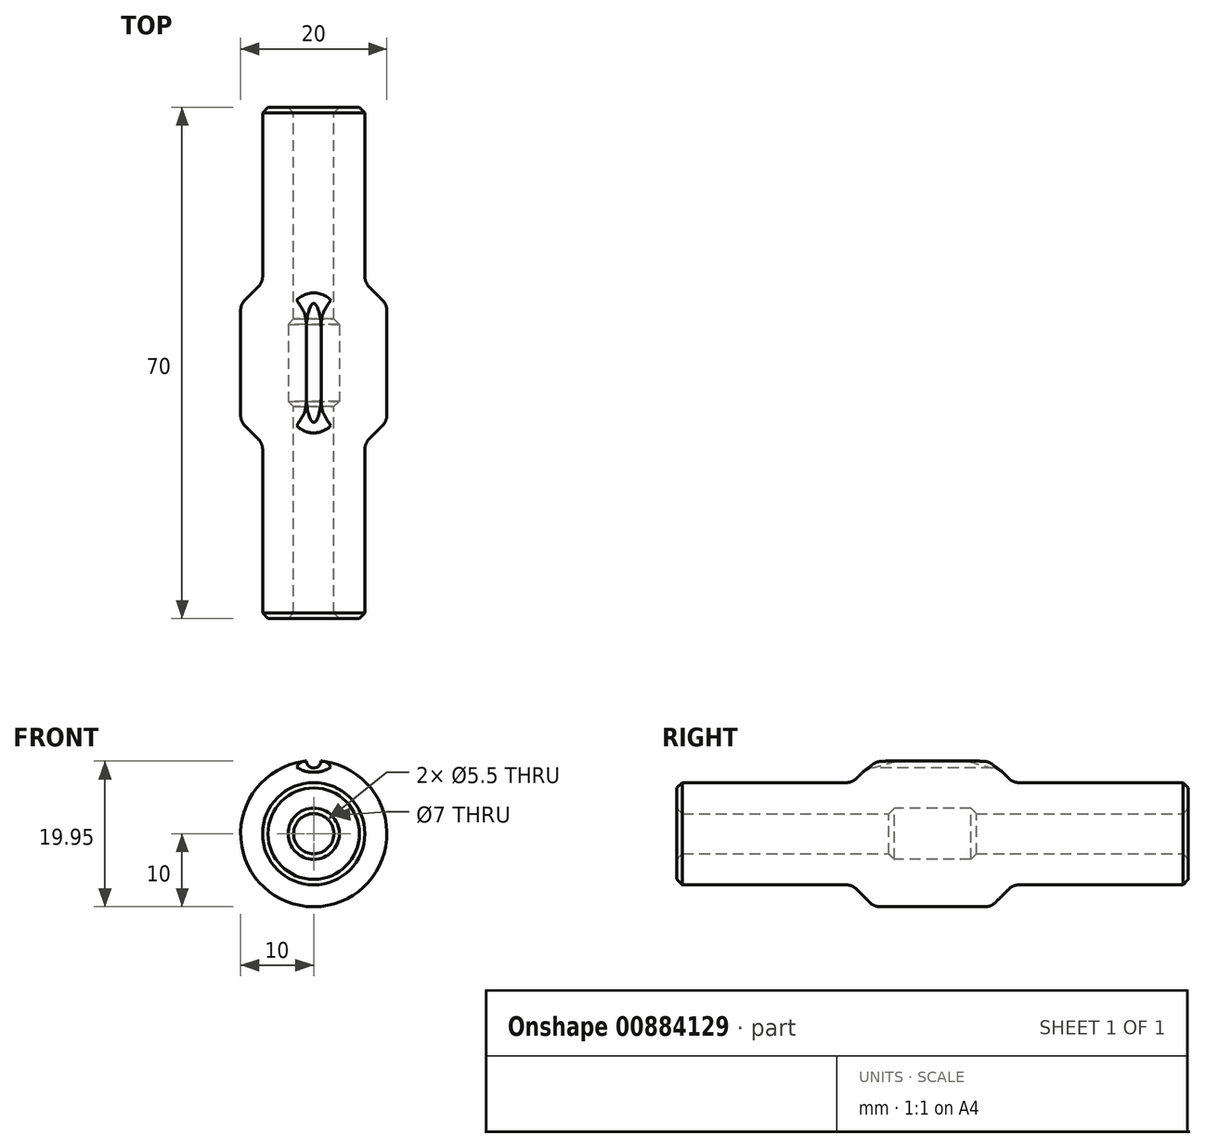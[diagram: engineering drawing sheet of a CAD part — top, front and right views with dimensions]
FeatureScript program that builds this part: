
annotation { "Feature Type Name" : "Feature", "Feature Type Description" : "" }
export const myFeature = defineFeature(function(context is Context, id is Id, definition is map)
    precondition{}
    {
        {
            var Q0;
            Q0=qCreatedBy(makeId("Front.planeOp"),FACE);
            var sketch = newSketch(context, id + "F0", { "sketchPlane" : qUnion([Q0])});
            skCircle(sketch, "E0", {"center": v(0, 0) * mm, "radius": 7 * mm});
            skCircle(sketch, "E1", {"center": v(0, 0) * mm, "radius": 2.75 * mm});
            skSolve(sketch);
        }
        {
            var Q0;
            Q0 = qSketchRegion(id + "F0", true);
            extrude(context, id + "F1", {"entities" : qUnion([Q0]), "endBound" : BoundingType.SYMMETRIC, "depth" : 70 * mm, "offsetDistance" : 25.4 * mm});
        }
        {
            var Q0;
            Q0=qCreatedBy(makeId("Front.planeOp"),FACE);
            var sketch = newSketch(context, id + "F2", { "sketchPlane" : qUnion([Q0])});
            skCircle(sketch, "E2", {"center": v(0, 0) * mm, "radius": 10 * mm});
            skCircle(sketch, "E3.0", {"center": v(0, 0) * mm, "radius": 2.75 * mm});
            skSolve(sketch);
        }
        {
            var Q0;
            Q0 = qSketchRegion(id + "F2", true);
            extrude(context, id + "F3", {"entities" : qUnion([Q0]), "operationType" : NewBodyOperationType.ADD, "endBound" : BoundingType.SYMMETRIC, "depth" : 16 * mm, "offsetDistance" : 25.4 * mm});
        }
        {
            var Q0;
            Q0=qCreatedBy(makeId("Front.planeOp"),FACE);
            var sketch = newSketch(context, id + "F4", { "sketchPlane" : qUnion([Q0])});
            skCircle(sketch, "E4.0", {"center": v(0, 0) * mm, "radius": 3.5 * mm});
            skSolve(sketch);
        }
        {
            var Q0;
            Q0 = qSketchRegion(id + "F4", true);
            var Q1;
            Q1=makeQuery(id+"F3.opExtrude","CAP_FACE",FACE,{"disambiguationData":[OSD([sQuery(id+"F2.wireOp",EDGE,"E2"),sQuery(id+"F2.wireOp",EDGE,"E3.0")])],"isStart":true});
            extrude(context, id + "F5", {"entities" : qUnion([Q0]), "operationType" : NewBodyOperationType.REMOVE, "endBound" : BoundingType.SYMMETRIC, "oppositeDirection" : true, "depth" : 12 * mm, "endBoundEntityFace" : qUnion([Q1]), "offsetDistance" : 25.4 * mm});
        }
        {
            var Q0;
            Q0=makeQuery(id+"F3.boolean.opBoolean","INTERSECT",EDGE,{"derivedFrom":[makeQuery(id+"F1.opExtrude","SWEPT_FACE",FACE,{"disambiguationData":[OSD([sQuery(id+"F0.wireOp",EDGE,"E0")])]}),makeQuery(id+"F3.opExtrude","CAP_FACE",FACE,{"disambiguationData":[OSD([sQuery(id+"F2.wireOp",EDGE,"E2"),sQuery(id+"F2.wireOp",EDGE,"E3.0")])],"isStart":false})]});
            var Q1;
            Q1=makeQuery(id+"F3.boolean.opBoolean","INTERSECT",EDGE,{"derivedFrom":[makeQuery(id+"F1.opExtrude","SWEPT_FACE",FACE,{"disambiguationData":[OSD([sQuery(id+"F0.wireOp",EDGE,"E0")])]}),makeQuery(id+"F3.opExtrude","CAP_FACE",FACE,{"disambiguationData":[OSD([sQuery(id+"F2.wireOp",EDGE,"E2"),sQuery(id+"F2.wireOp",EDGE,"E3.0")])],"isStart":true})]});
            chamfer(context, id + "F6", {"entities" : qUnion([Q0, Q1]), "width" : 3 * mm, "tangentPropagation" : true});
        }
        {
            var Q0;
            Q0=makeQuery(id+"F1.opExtrude","CAP_FACE",FACE,{"disambiguationData":[OSD([sQuery(id+"F0.wireOp",EDGE,"E0"),sQuery(id+"F0.wireOp",EDGE,"E1")])],"isStart":false});
            var sketch = newSketch(context, id + "F7", { "sketchPlane" : qUnion([Q0])});
            skCircle(sketch, "E5", {"center": v(0, 10) * mm, "radius": 1 * mm});
            skSolve(sketch);
        }
        {
            var Q0;
            Q0 = qSketchRegion(id + "F7", true);
            var Q1;
            Q1=makeQuery(id+"F3.opExtrude","CAP_FACE",FACE,{"disambiguationData":[OSD([sQuery(id+"F2.wireOp",EDGE,"E2"),sQuery(id+"F2.wireOp",EDGE,"E3.0")])],"isStart":true});
            var Q2;
            Q2=makeQuery(id+"F3.opExtrude","CAP_FACE",FACE,{"disambiguationData":[OSD([sQuery(id+"F2.wireOp",EDGE,"E2"),sQuery(id+"F2.wireOp",EDGE,"E3.0")])],"isStart":false});
            extrude(context, id + "F8", {"entities" : qUnion([Q0]), "operationType" : NewBodyOperationType.REMOVE, "endBound" : BoundingType.THROUGH_ALL, "oppositeDirection" : true, "depth" : 25.4 * mm, "endBoundEntityFace" : qUnion([Q1]), "offsetDistance" : 25.4 * mm});
        }
        {
            var Q0;
            Q0=makeQuery(id+"F1.opExtrude","CAP_EDGE",EDGE,{"disambiguationData":[OSD([sQuery(id+"F0.wireOp",EDGE,"E1")])],"isStart":false});
            var Q1;
            Q1=makeQuery(id+"F1.opExtrude","CAP_EDGE",EDGE,{"disambiguationData":[OSD([sQuery(id+"F0.wireOp",EDGE,"E1")])],"isStart":true});
            var Q2;
            Q2=makeQuery(id+"F5.boolean.opBoolean","COPY",EDGE,{"derivedFrom":makeQuery(id+"F5.opExtrude","CAP_EDGE",EDGE,{"disambiguationData":[OSD([sQuery(id+"F4.wireOp",EDGE,"E4.0")])],"isStart":true})});
            var Q3;
            Q3=makeQuery(id+"F5.boolean.opBoolean","COPY",EDGE,{"derivedFrom":makeQuery(id+"F5.opExtrude","CAP_EDGE",EDGE,{"disambiguationData":[OSD([sQuery(id+"F4.wireOp",EDGE,"E4.0")])],"isStart":false})});
            var Q4;
            Q4=makeQuery(id+"F1.opExtrude","CAP_EDGE",EDGE,{"disambiguationData":[OSD([sQuery(id+"F0.wireOp",EDGE,"E0")])],"isStart":false});
            var Q5;
            Q5=makeQuery(id+"F1.opExtrude","CAP_EDGE",EDGE,{"disambiguationData":[OSD([sQuery(id+"F0.wireOp",EDGE,"E0")])],"isStart":true});
            chamfer(context, id + "F9", {"entities" : qUnion([Q0, Q1, Q2, Q3, Q4, Q5]), "width" : .75 * mm, "tangentPropagation" : true});
        }
        {
            var Q0;
            {var subQ0=sQuery(id+"F0.wireOp",EDGE,"E0");var subQ1=makeQuery(id+"F3.opExtrude","CAP_FACE",FACE,{"disambiguationData":[OSD([sQuery(id+"F2.wireOp",EDGE,"E2"),sQuery(id+"F2.wireOp",EDGE,"E3.0")])],"isStart":false});var subQ2=makeQuery(id+"F1.opExtrude","SWEPT_FACE",FACE,{"disambiguationData":[OSD([subQ0])]});Q0=makeQuery(id+"F6.opChamfer","BLEND_EDGE",EDGE,{"blendedFrom":[makeQuery(id+"F3.boolean.opBoolean","INTERSECT",EDGE,{"derivedFrom":[subQ2,subQ1]}),makeQuery(id+"F3.boolean.opBoolean","SPLIT",FACE,{"disambiguationData":[TD([makeQuery(id+"F1.opExtrude","CAP_FACE",FACE,{"disambiguationData":[OSD([subQ0,sQuery(id+"F0.wireOp",EDGE,"E1")])],"isStart":false})])],"derivedFrom":subQ2})],"blendedInto":[makeQuery(id+"F3.boolean.opBoolean","SPLIT",FACE,{"disambiguationData":[TD([makeQuery(id+"F1.opExtrude","CAP_FACE",FACE,{"disambiguationData":[OSD([subQ0,sQuery(id+"F0.wireOp",EDGE,"E1")])],"isStart":false})])],"derivedFrom":subQ2})]});}
            var Q1;
            {var subQ0=sQuery(id+"F0.wireOp",EDGE,"E0");var subQ1=makeQuery(id+"F3.opExtrude","CAP_FACE",FACE,{"disambiguationData":[OSD([sQuery(id+"F2.wireOp",EDGE,"E2"),sQuery(id+"F2.wireOp",EDGE,"E3.0")])],"isStart":true});var subQ2=makeQuery(id+"F1.opExtrude","SWEPT_FACE",FACE,{"disambiguationData":[OSD([subQ0])]});Q1=makeQuery(id+"F6.opChamfer","BLEND_EDGE",EDGE,{"blendedFrom":[makeQuery(id+"F3.boolean.opBoolean","INTERSECT",EDGE,{"derivedFrom":[subQ2,subQ1]}),makeQuery(id+"F3.boolean.opBoolean","SPLIT",FACE,{"disambiguationData":[TD([makeQuery(id+"F1.opExtrude","CAP_FACE",FACE,{"disambiguationData":[OSD([subQ0,sQuery(id+"F0.wireOp",EDGE,"E1")])],"isStart":true})])],"derivedFrom":subQ2})],"blendedInto":[makeQuery(id+"F3.boolean.opBoolean","SPLIT",FACE,{"disambiguationData":[TD([makeQuery(id+"F1.opExtrude","CAP_FACE",FACE,{"disambiguationData":[OSD([subQ0,sQuery(id+"F0.wireOp",EDGE,"E1")])],"isStart":true})])],"derivedFrom":subQ2})]});}
            var Q2;
            {var subQ0=sQuery(id+"F2.wireOp",EDGE,"E3.0");var subQ1=sQuery(id+"F2.wireOp",EDGE,"E2");var subQ2=sQuery(id+"F0.wireOp",EDGE,"E0");Q2=makeQuery(id+"F6.opChamfer","BLEND_FACE",FACE,{"disambiguationData":[OSD([subQ2,subQ1,subQ0]),TDD([makeQuery(id+"F3.boolean.opBoolean","INTERSECT",EDGE,{"derivedFrom":[makeQuery(id+"F1.opExtrude","SWEPT_FACE",FACE,{"disambiguationData":[OSD([subQ2])]}),makeQuery(id+"F3.opExtrude","CAP_FACE",FACE,{"disambiguationData":[OSD([subQ1,subQ0])],"isStart":false})]})])]});}
            var Q3;
            {var subQ0=sQuery(id+"F2.wireOp",EDGE,"E3.0");var subQ1=sQuery(id+"F2.wireOp",EDGE,"E2");var subQ2=sQuery(id+"F0.wireOp",EDGE,"E0");Q3=makeQuery(id+"F6.opChamfer","BLEND_FACE",FACE,{"disambiguationData":[OSD([subQ2,subQ1,subQ0]),TDD([makeQuery(id+"F3.boolean.opBoolean","INTERSECT",EDGE,{"derivedFrom":[makeQuery(id+"F1.opExtrude","SWEPT_FACE",FACE,{"disambiguationData":[OSD([subQ2])]}),makeQuery(id+"F3.opExtrude","CAP_FACE",FACE,{"disambiguationData":[OSD([subQ1,subQ0])],"isStart":true})]})])]});}
            fillet(context, id + "F10", {"entities" : qUnion([Q0, Q1, Q2, Q3]), "radius" : 2 * mm, "tangentPropagation" : true, "allowEdgeOverflow" : false});
        }
    });
